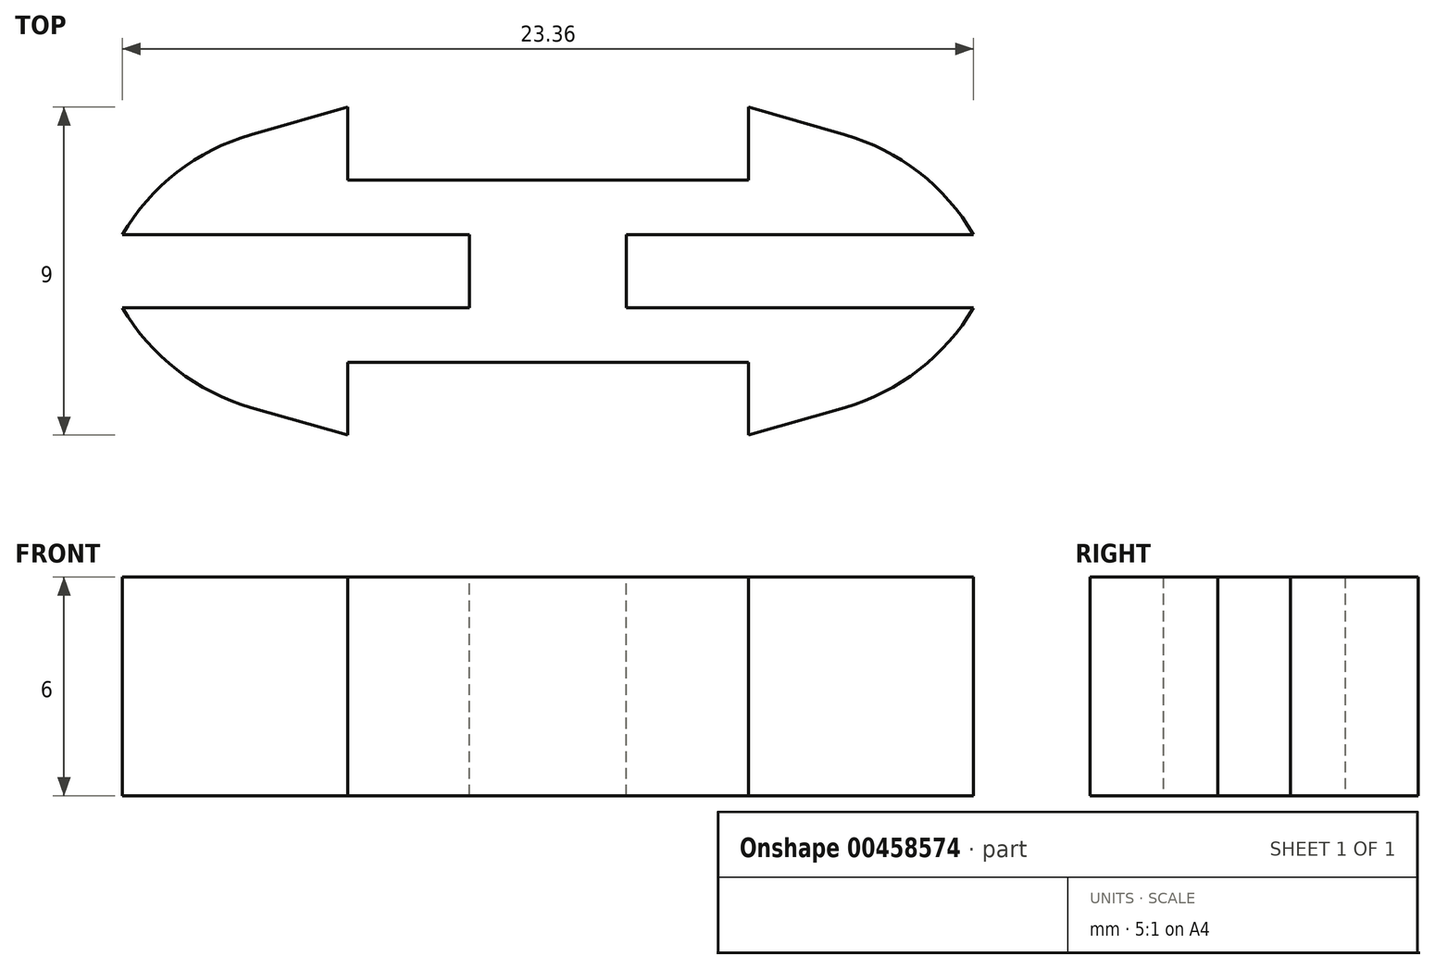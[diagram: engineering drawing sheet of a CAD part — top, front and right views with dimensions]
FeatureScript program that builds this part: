
annotation { "Feature Type Name" : "Feature", "Feature Type Description" : "" }
export const myFeature = defineFeature(function(context is Context, id is Id, definition is map)
    precondition{}
    {
        {
            var Q0;
            Q0=qCreatedBy(makeId("Top.planeOp"),FACE);
            var sketch = newSketch(context, id + "F0", { "sketchPlane" : qUnion([Q0])});
            skLineSegment(sketch, "E0.bottom", {"start": v(-7, 5) * mm, "end": v(18, 5) * mm});
            skLineSegment(sketch, "E0.top", {"start": v(-7, 0) * mm, "end": v(18, 0) * mm});
            skLineSegment(sketch, "E0.left", {"start": v(-7, 5) * mm, "end": v(-7, 0) * mm});
            skLineSegment(sketch, "E0.right", {"start": v(18, 5) * mm, "end": v(18, 0) * mm});
            skLineSegment(sketch, "E1", {"start": v(-7, 5) * mm, "end": v(0, 7) * mm});
            skLineSegment(sketch, "E2", {"start": v(0, 7) * mm, "end": v(0, 5) * mm});
            skLineSegment(sketch, "E3", {"start": v(18, 5) * mm, "end": v(11, 7) * mm});
            skLineSegment(sketch, "E4", {"start": v(11, 7) * mm, "end": v(11, 5) * mm});
            skLineSegment(sketch, "E5", {"start": v(-7, 0) * mm, "end": v(0, -2) * mm});
            skLineSegment(sketch, "E6", {"start": v(18, 0) * mm, "end": v(11, -2) * mm});
            skLineSegment(sketch, "E7", {"start": v(11, -2) * mm, "end": v(11, 0) * mm});
            skLineSegment(sketch, "E8", {"start": v(0, -2) * mm, "end": v(0, 0) * mm});
            skSolve(sketch);
        }
        {
            var Q0;
            Q0 = qSketchRegion(id + "F0", true);
            extrude(context, id + "F1", {"entities" : qUnion([Q0]), "depth" : 6 * mm, "offsetDistance" : 25 * mm});
        }
        {
            var Q0;
            Q0=makeQuery(id+"F1.opExtrude","SWEPT_EDGE",EDGE,{"disambiguationData":[OSD([sQuery(id+"F0.wireOp",EDGE,"E0.bottom"),sQuery(id+"F0.wireOp",EDGE,"E0.left"),sQuery(id+"F0.wireOp",EDGE,"E1")])]});
            var Q1;
            Q1=makeQuery(id+"F1.opExtrude","SWEPT_EDGE",EDGE,{"disambiguationData":[OSD([sQuery(id+"F0.wireOp",EDGE,"E0.top"),sQuery(id+"F0.wireOp",EDGE,"E0.left"),sQuery(id+"F0.wireOp",EDGE,"E5")])]});
            var Q2;
            Q2=makeQuery(id+"F1.opExtrude","SWEPT_EDGE",EDGE,{"disambiguationData":[OSD([sQuery(id+"F0.wireOp",EDGE,"E0.bottom"),sQuery(id+"F0.wireOp",EDGE,"E0.right"),sQuery(id+"F0.wireOp",EDGE,"E3")])]});
            var Q3;
            Q3=makeQuery(id+"F1.opExtrude","SWEPT_EDGE",EDGE,{"disambiguationData":[OSD([sQuery(id+"F0.wireOp",EDGE,"E0.top"),sQuery(id+"F0.wireOp",EDGE,"E0.right"),sQuery(id+"F0.wireOp",EDGE,"E6")])]});
            fillet(context, id + "F2", {"entities" : qUnion([Q0, Q1, Q2, Q3]), "radius" : 6 * mm, "tangentPropagation" : true, "allowEdgeOverflow" : false});
        }
        {
            var Q0;
            Q0=makeQuery(id+"F1.opExtrude","CAP_FACE",FACE,{"disambiguationData":[OSD([sQuery(id+"F0.wireOp",EDGE,"E0.bottom"),sQuery(id+"F0.wireOp",EDGE,"E0.top"),sQuery(id+"F0.wireOp",EDGE,"E0.left"),sQuery(id+"F0.wireOp",EDGE,"E0.right"),sQuery(id+"F0.wireOp",EDGE,"E1"),sQuery(id+"F0.wireOp",EDGE,"E2"),sQuery(id+"F0.wireOp",EDGE,"E3"),sQuery(id+"F0.wireOp",EDGE,"E4"),sQuery(id+"F0.wireOp",EDGE,"E5"),sQuery(id+"F0.wireOp",EDGE,"E6"),sQuery(id+"F0.wireOp",EDGE,"E7"),sQuery(id+"F0.wireOp",EDGE,"E8")])],"isStart":false});
            var sketch = newSketch(context, id + "F3", { "sketchPlane" : qUnion([Q0])});
            skLineSegment(sketch, "E9.bottom", {"start": v(3.35, 3.5) * mm, "end": v(-9.27, 3.5) * mm});
            skLineSegment(sketch, "E9.top", {"start": v(3.35, 1.5) * mm, "end": v(-9.27, 1.5) * mm});
            skLineSegment(sketch, "E9.left", {"start": v(3.35, 3.5) * mm, "end": v(3.35, 1.5) * mm});
            skLineSegment(sketch, "E9.right", {"start": v(-9.27, 3.5) * mm, "end": v(-9.27, 1.5) * mm});
            skLineSegment(sketch, "E10.bottom", {"start": v(7.65, 3.5) * mm, "end": v(22.98, 3.5) * mm});
            skLineSegment(sketch, "E10.top", {"start": v(7.65, 1.5) * mm, "end": v(22.98, 1.5) * mm});
            skLineSegment(sketch, "E10.left", {"start": v(7.65, 3.5) * mm, "end": v(7.65, 1.5) * mm});
            skLineSegment(sketch, "E10.right", {"start": v(22.98, 3.5) * mm, "end": v(22.98, 1.5) * mm});
            skSolve(sketch);
        }
        {
            var Q0;
            Q0 = qSketchRegion(id + "F3", true);
            extrude(context, id + "F4", {"entities" : qUnion([Q0]), "operationType" : NewBodyOperationType.REMOVE, "oppositeDirection" : true, "depth" : 6 * mm, "offsetDistance" : 25 * mm});
        }
    });
